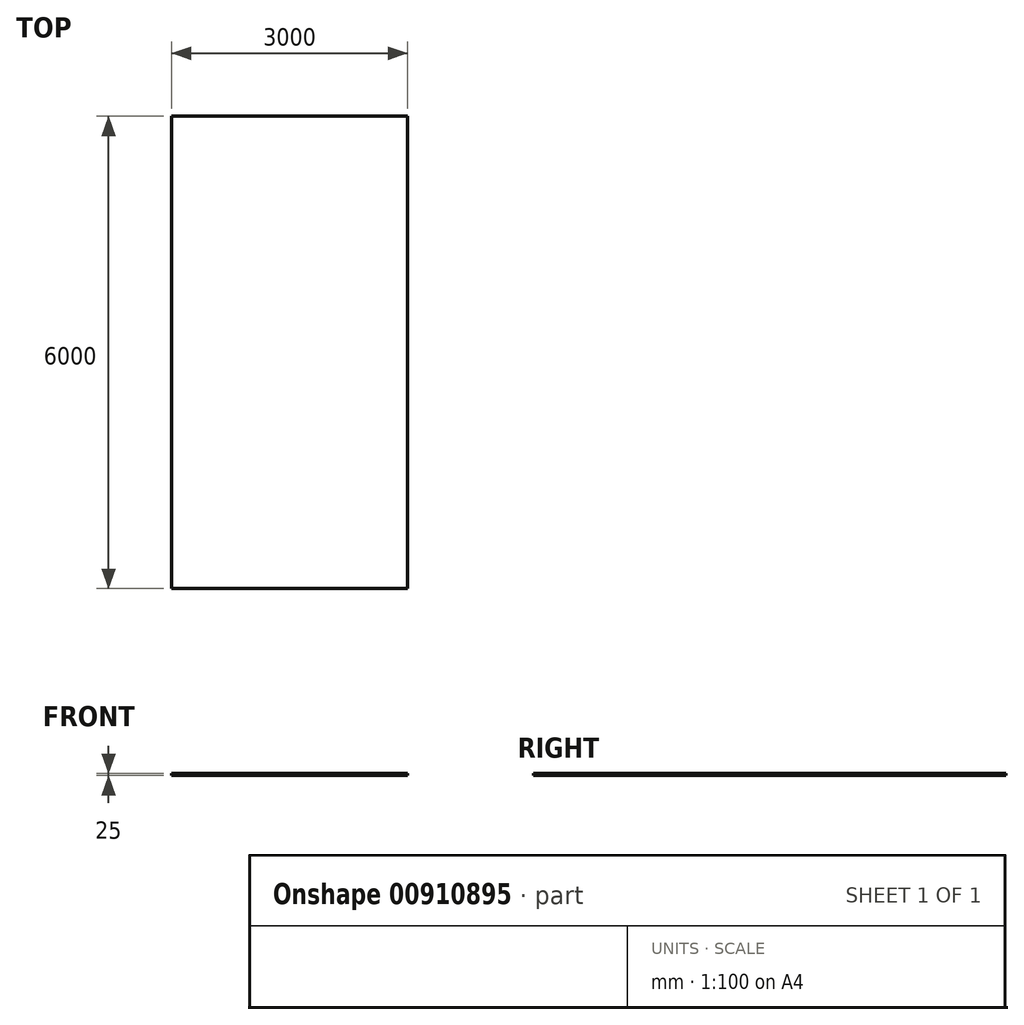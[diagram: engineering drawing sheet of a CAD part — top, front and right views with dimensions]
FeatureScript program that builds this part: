
annotation { "Feature Type Name" : "Feature", "Feature Type Description" : "" }
export const myFeature = defineFeature(function(context is Context, id is Id, definition is map)
    precondition{}
    {
        {
            var Q0;
            Q0=qCreatedBy(makeId("Top.planeOp"),FACE);
            var sketch = newSketch(context, id + "F0", { "sketchPlane" : qUnion([Q0])});
            skLineSegment(sketch, "E0.bottom", {"start": v(-3335.6, 2939.06) * mm, "end": v(-335.6, 2939.06) * mm});
            skLineSegment(sketch, "E0.top", {"start": v(-3335.6, -3060.94) * mm, "end": v(-335.6, -3060.94) * mm});
            skLineSegment(sketch, "E0.left", {"start": v(-3335.6, 2939.06) * mm, "end": v(-3335.6, -3060.94) * mm});
            skLineSegment(sketch, "E0.right", {"start": v(-335.6, 2939.06) * mm, "end": v(-335.6, -3060.94) * mm});
            skSolve(sketch);
        }
        {
            var Q0;
            Q0=makeQuery(id+"F0.imprint","IMPRINT",FACE,{"disambiguationData":[TD([[makeQuery(id+"F0.imprint","IMPRINT",EDGE,{"derivedFrom":sQuery(id+"F0.wireOp",EDGE,"E0.bottom")}),-1.0]])]});
            extrude(context, id + "F1", {"entities" : qUnion([Q0]), "oppositeDirection" : true, "depth" : 25 * mm, "offsetDistance" : 25 * mm});
        }
    });
